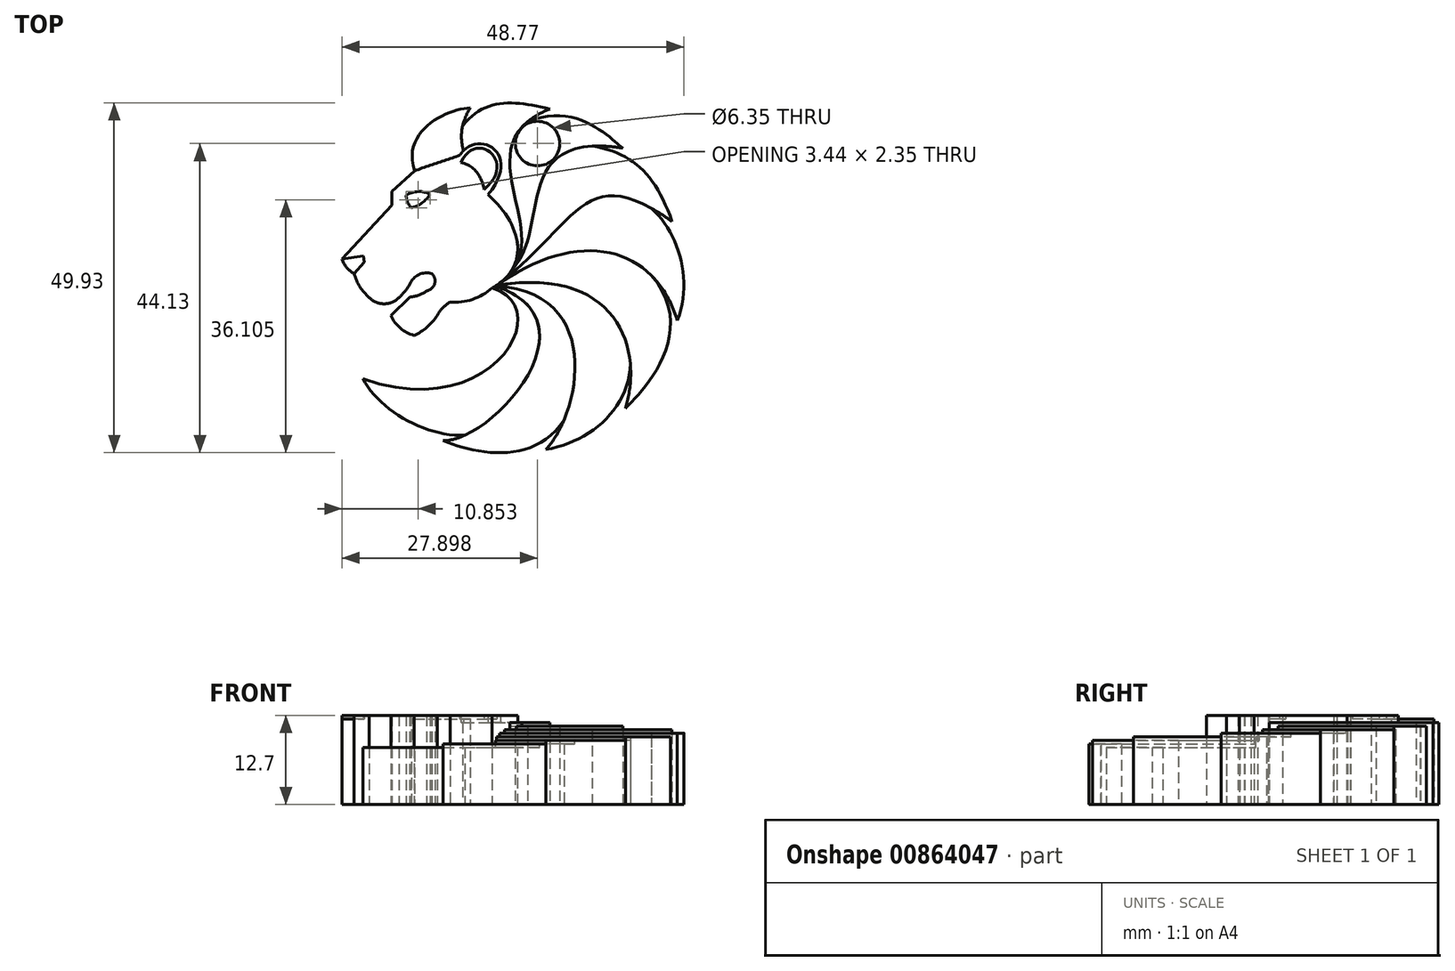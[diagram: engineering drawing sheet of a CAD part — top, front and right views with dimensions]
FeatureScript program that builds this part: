
annotation { "Feature Type Name" : "Feature", "Feature Type Description" : "" }
export const myFeature = defineFeature(function(context is Context, id is Id, definition is map)
    precondition{}
    {
        {
            var Q0;
            Q0=qCreatedBy(makeId("Top.planeOp"),FACE);
            var sketch = newSketch(context, id + "F0", { "sketchPlane" : qUnion([Q0])});
            skFitSpline(sketch, "E0", {"points": [v(-11.17, 15.49) * mm, v(-3.2, 24.48) * mm], "startDerivative": vector(-5.74, 17.74) * mm, "endDerivative": vector(9.44, 0.42) * mm});
            skFitSpline(sketch, "E1", {"points": [v(-3.2, 24.48) * mm, v(-4.16, 18.37) * mm], "startDerivative": vector(-4.63, -7.44) * mm, "endDerivative": vector(1.4, -4.65) * mm});
            skFitSpline(sketch, "E2", {"points": [v(-4.3, 21.92) * mm, v(8.12, 24.3) * mm], "startDerivative": vector(9.68, 12.41) * mm, "endDerivative": vector(14.74, -3.6) * mm});
            skFitSpline(sketch, "E3", {"points": [v(8.12, 24.3) * mm, v(2.46, 0.93) * mm], "startDerivative": vector(-37.26, -15.04) * mm, "endDerivative": vector(-17.73, -19.22) * mm});
            skFitSpline(sketch, "E4", {"points": [v(4.97, 22.5) * mm, v(18.56, 18.74) * mm], "startDerivative": vector(22.85, 9.47) * mm, "endDerivative": vector(2.68, -1.02) * mm});
            skFitSpline(sketch, "E5", {"points": [v(18.56, 18.74) * mm, v(3.37, 2.21) * mm], "startDerivative": vector(-47.21, 7.34) * mm, "endDerivative": vector(-13.68, -17.2) * mm});
            skFitSpline(sketch, "E6", {"points": [v(14.17, 19) * mm, v(25.57, 8.25) * mm], "startDerivative": vector(17.93, -2.85) * mm, "endDerivative": vector(7.02, -19.74) * mm});
            skFitSpline(sketch, "E7", {"points": [v(25.57, 8.25) * mm, v(1.63, 0) * mm], "startDerivative": vector(-37.02, 26.3) * mm, "endDerivative": vector(-32, -25.23) * mm});
            skFitSpline(sketch, "E8", {"points": [v(22.65, 10.13) * mm, v(26.33, -5.88) * mm], "startDerivative": vector(11.59, -10.64) * mm, "endDerivative": vector(-6.75, -17.65) * mm});
            skFitSpline(sketch, "E9", {"points": [v(26.33, -5.88) * mm, v(0.53, -0.85) * mm], "startDerivative": vector(-9.04, 30.15) * mm, "endDerivative": vector(-37.82, -26.43) * mm});
            skFitSpline(sketch, "E10", {"points": [v(22.63, 0.55) * mm, v(18.92, -18.4) * mm], "startDerivative": vector(21.92, -25.56) * mm, "endDerivative": vector(-4.38, -4.47) * mm});
            skFitSpline(sketch, "E11", {"points": [v(18.92, -18.4) * mm, v(0.51, -0.86) * mm], "startDerivative": vector(7.83, 25) * mm, "endDerivative": vector(-52.23, -8.41) * mm});
            skFitSpline(sketch, "E12", {"points": [v(19.61, -12) * mm, v(7.6, -24.27) * mm], "startDerivative": vector(-0.32, -19.2) * mm, "endDerivative": vector(-18.73, -3.03) * mm});
            skFitSpline(sketch, "E13", {"points": [v(7.6, -24.27) * mm, v(0.41, -0.93) * mm], "startDerivative": vector(14.87, 16.04) * mm, "endDerivative": vector(-46.34, 2.64) * mm});
            skFitSpline(sketch, "E14", {"points": [v(10.15, -20.1) * mm, v(-7.07, -23.03) * mm], "startDerivative": vector(-12.89, -19.52) * mm, "endDerivative": vector(-14.06, 5.82) * mm});
            skFitSpline(sketch, "E15", {"points": [v(-7.07, -23.03) * mm, v(0.38, -0.96) * mm], "startDerivative": vector(21.2, -0.2) * mm, "endDerivative": vector(-44.64, 14.98) * mm});
            skFitSpline(sketch, "E16", {"points": [v(-18.51, -14.19) * mm, v(-4, -22.26) * mm], "startDerivative": vector(6.81, -13.35) * mm, "endDerivative": vector(16.4, 0.89) * mm});
            skFitSpline(sketch, "E17", {"points": [v(-18.51, -14.19) * mm, v(-0.1, -1.23) * mm], "startDerivative": vector(55.54, -19.7) * mm, "endDerivative": vector(-28.08, 7.97) * mm});
            skLineSegment(sketch, "E18", {"start": v(-14.38, 10.58) * mm, "end": v(-21.51, 2.89) * mm});
            skLineSegment(sketch, "E19", {"start": v(-14.38, 10.58) * mm, "end": v(-14.38, 12.56) * mm});
            skLineSegment(sketch, "E20", {"start": v(-14.38, 12.56) * mm, "end": v(-11.17, 15.49) * mm});
            skLineSegment(sketch, "E21", {"start": v(-14.52, -5.17) * mm, "end": v(-11.79, -2.52) * mm});
            skArc(sketch, "E22", {"start": v(-12.38, 12) * mm, "mid": v(-12.16, 11.04) * mm, "end": v(-11.67, 10.18) * mm});
            skArc(sketch, "E23", {"start": v(-11.67, 10.18) * mm, "mid": v(-10.11, 10.9) * mm, "end": v(-8.94, 12.15) * mm});
            skArc(sketch, "E24", {"start": v(-8.94, 12.15) * mm, "mid": v(-10.68, 12.53) * mm, "end": v(-12.38, 12) * mm});
            skArc(sketch, "E25", {"start": v(-21.51, 2.89) * mm, "mid": v(-20.84, 1.7) * mm, "end": v(-19.78, 0.83) * mm});
            skArc(sketch, "E26", {"start": v(-19.78, 0.83) * mm, "mid": v(-18.95, -1.05) * mm, "end": v(-17.61, -2.61) * mm});
            skArc(sketch, "E27", {"start": v(-17.61, -2.61) * mm, "mid": v(-15.5, -3.5) * mm, "end": v(-13.39, -2.61) * mm});
            skArc(sketch, "E28", {"start": v(-14.52, -5.17) * mm, "mid": v(-13.2, -6.97) * mm, "end": v(-11.22, -8) * mm});
            skArc(sketch, "E29", {"start": v(-11.22, -8) * mm, "mid": v(-9.37, -6.83) * mm, "end": v(-7.94, -5.17) * mm});
            skArc(sketch, "E30", {"start": v(-6.1, -3.27) * mm, "mid": v(-7.15, -4.1) * mm, "end": v(-7.94, -5.17) * mm});
            skArc(sketch, "E31", {"start": v(-6.1, -3.27) * mm, "mid": v(-2.89, -2.86) * mm, "end": v(-0.1, -1.23) * mm});
            skArc(sketch, "E32", {"start": v(-13.39, -2.61) * mm, "mid": v(-12.54, -1.7) * mm, "end": v(-11.84, -0.7) * mm});
            skArc(sketch, "E33", {"start": v(-8.67, 0.8) * mm, "mid": v(-10.54, 0.68) * mm, "end": v(-11.84, -0.7) * mm});
            skArc(sketch, "E34", {"start": v(-9.44, -1.65) * mm, "mid": v(-8.3, -0.66) * mm, "end": v(-8.67, 0.8) * mm});
            skArc(sketch, "E35", {"start": v(-11.79, -2.52) * mm, "mid": v(-10.55, -2.26) * mm, "end": v(-9.44, -1.65) * mm});
            skFitSpline(sketch, "E36", {"points": [v(-0.1, -1.23) * mm, v(-0.7, 12.08) * mm], "startDerivative": vector(17.47, 9.64) * mm, "endDerivative": vector(-13.78, 11.7) * mm});
            skFitSpline(sketch, "E37", {"points": [v(-11.17, 15.49) * mm, v(-4.66, 17.73) * mm], "startDerivative": vector(6.4, 2.3) * mm, "endDerivative": vector(6.4, 2.3) * mm});
            skLineSegment(sketch, "E38", {"start": v(-21.51, 2.89) * mm, "end": v(-18.44, 3.32) * mm});
            skLineSegment(sketch, "E39", {"start": v(-18.44, 3.32) * mm, "end": v(-18.32, 2.44) * mm});
            skLineSegment(sketch, "E40", {"start": v(-18.32, 2.44) * mm, "end": v(-19.78, 0.83) * mm});
            skLineSegment(sketch, "E41", {"start": v(-18.44, 3.32) * mm, "end": v(-11.67, 10.18) * mm});
            skFitSpline(sketch, "E42", {"points": [v(-5.1, 16.82) * mm, v(-0.7, 12.08) * mm], "startDerivative": vector(5.58, 15.8) * mm, "endDerivative": vector(-16.44, -19.38) * mm});
            skFitSpline(sketch, "E43", {"points": [v(-4.56, 16.67) * mm, v(-1.23, 12.83) * mm], "startDerivative": vector(6.77, 14.53) * mm, "endDerivative": vector(-14.42, -11.84) * mm});
            skFitSpline(sketch, "E44", {"points": [v(-4.56, 16.67) * mm, v(-1.23, 12.83) * mm], "startDerivative": vector(6.2, -1.24) * mm, "endDerivative": vector(0.83, -4.86) * mm});
            skPoint(sketch, "E45", {"position": v(6.39, 19.38) * mm});
            skSolve(sketch);
        }
        {
            var Q0;
            Q0=makeQuery(id+"F0.imprint","IMPRINT",FACE,{"disambiguationData":[TD([[makeQuery(id+"F0.imprint","IMPRINT",EDGE,{"derivedFrom":sQuery(id+"F0.wireOp",EDGE,"E18")}),1.0]])]});
            extrude(context, id + "F1", {"entities" : qUnion([Q0]), "depth" : 12.7 * mm, "offsetDistance" : 25.4 * mm});
        }
        {
            var Q0;
            {var subQ4=sQuery(id+"F0.wireOp",EDGE,"E0");Q0=makeQuery(id+"F0.imprint","IMPRINT",FACE,{"disambiguationData":[TD([[makeQuery(id+"F0.imprint","IMPRINT",EDGE,{"derivedFrom":subQ4}),-1.0]])]});}
            var Q1;
            Q1=makeQuery(id+"F0.imprint","IMPRINT",FACE,{"disambiguationData":[TD([[makeQuery(id+"F0.imprint","IMPRINT",EDGE,{"derivedFrom":sQuery(id+"F0.wireOp",EDGE,"E43")}),-1.0]])]});
            var Q2;
            Q2=makeQuery(id+"F0.imprint","IMPRINT",FACE,{"disambiguationData":[TD([[makeQuery(id+"F0.imprint","IMPRINT",EDGE,{"derivedFrom":sQuery(id+"F0.wireOp",EDGE,"E25")}),1.0]])]});
            extrude(context, id + "F2", {"entities" : qUnion([Q0, Q1, Q2]), "operationType" : NewBodyOperationType.ADD, "depth" : 12.2 * mm, "offsetDistance" : 25.4 * mm});
        }
        {
            var Q0;
            {var subQ3=sQuery(id+"F0.wireOp",EDGE,"E2");Q0=makeQuery(id+"F0.imprint","IMPRINT",FACE,{"disambiguationData":[TD([[makeQuery(id+"F0.imprint","IMPRINT",EDGE,{"derivedFrom":subQ3}),-1.0]])]});}
            extrude(context, id + "F3", {"entities" : qUnion([Q0]), "operationType" : NewBodyOperationType.ADD, "depth" : 11.68 * mm, "offsetDistance" : 25.4 * mm});
        }
        {
            var Q0;
            {var subQ0=sQuery(id+"F0.wireOp",EDGE,"E4");Q0=makeQuery(id+"F0.imprint","IMPRINT",FACE,{"disambiguationData":[TD([[makeQuery(id+"F0.imprint","IMPRINT",EDGE,{"derivedFrom":subQ0}),-1.0]])]});}
            extrude(context, id + "F4", {"entities" : qUnion([Q0]), "operationType" : NewBodyOperationType.ADD, "depth" : 11.18 * mm, "offsetDistance" : 25.4 * mm});
        }
        {
            var Q0;
            {var subQ0=sQuery(id+"F0.wireOp",EDGE,"E6");Q0=makeQuery(id+"F0.imprint","IMPRINT",FACE,{"disambiguationData":[TD([[makeQuery(id+"F0.imprint","IMPRINT",EDGE,{"derivedFrom":subQ0}),-1.0]])]});}
            extrude(context, id + "F5", {"entities" : qUnion([Q0]), "operationType" : NewBodyOperationType.ADD, "depth" : 10.67 * mm, "offsetDistance" : 25.4 * mm});
        }
        {
            var Q0;
            {var subQ4=sQuery(id+"F0.wireOp",EDGE,"E8");Q0=makeQuery(id+"F0.imprint","IMPRINT",FACE,{"disambiguationData":[TD([[makeQuery(id+"F0.imprint","IMPRINT",EDGE,{"derivedFrom":subQ4}),-1.0]])]});}
            extrude(context, id + "F6", {"entities" : qUnion([Q0]), "operationType" : NewBodyOperationType.ADD, "depth" : 10.16 * mm, "offsetDistance" : 25.4 * mm});
        }
        {
            var Q0;
            {var subQ4=sQuery(id+"F0.wireOp",EDGE,"E10");Q0=makeQuery(id+"F0.imprint","IMPRINT",FACE,{"disambiguationData":[TD([[makeQuery(id+"F0.imprint","IMPRINT",EDGE,{"derivedFrom":subQ4}),-1.0]])]});}
            extrude(context, id + "F7", {"entities" : qUnion([Q0]), "operationType" : NewBodyOperationType.ADD, "depth" : 9.65 * mm, "offsetDistance" : 25.4 * mm});
        }
        {
            var Q0;
            {var subQ4=sQuery(id+"F0.wireOp",EDGE,"E12");Q0=makeQuery(id+"F0.imprint","IMPRINT",FACE,{"disambiguationData":[TD([[makeQuery(id+"F0.imprint","IMPRINT",EDGE,{"derivedFrom":subQ4}),-1.0]])]});}
            extrude(context, id + "F8", {"entities" : qUnion([Q0]), "operationType" : NewBodyOperationType.ADD, "depth" : 9.14 * mm, "offsetDistance" : 25.4 * mm});
        }
        {
            var Q0;
            {var subQ6=sQuery(id+"F0.wireOp",EDGE,"E14");Q0=makeQuery(id+"F0.imprint","IMPRINT",FACE,{"disambiguationData":[TD([[makeQuery(id+"F0.imprint","IMPRINT",EDGE,{"derivedFrom":subQ6}),-1.0]])]});}
            extrude(context, id + "F9", {"entities" : qUnion([Q0]), "operationType" : NewBodyOperationType.ADD, "depth" : 8.64 * mm, "offsetDistance" : 25.4 * mm});
        }
        {
            var Q0;
            {var subQ3=sQuery(id+"F0.wireOp",EDGE,"E16");Q0=makeQuery(id+"F0.imprint","IMPRINT",FACE,{"disambiguationData":[TD([[makeQuery(id+"F0.imprint","IMPRINT",EDGE,{"derivedFrom":subQ3}),1.0]])]});}
            extrude(context, id + "F10", {"entities" : qUnion([Q0]), "operationType" : NewBodyOperationType.ADD, "depth" : 8.13 * mm, "offsetDistance" : 25.4 * mm});
        }
        {
            var Q0;
            Q0=sQuery(id+"F0.wireOp",VERTEX,"E45");
            var Q1;
            Q1=makeQuery(id+"F1.opExtrude","SWEPT_BODY",BODY,{"disambiguationData":[OSD([sQuery(id+"F0.wireOp",EDGE,"E18"),sQuery(id+"F0.wireOp",EDGE,"E19"),sQuery(id+"F0.wireOp",EDGE,"E20"),sQuery(id+"F0.wireOp",EDGE,"E21"),sQuery(id+"F0.wireOp",EDGE,"E22"),sQuery(id+"F0.wireOp",EDGE,"E23"),sQuery(id+"F0.wireOp",EDGE,"E24"),sQuery(id+"F0.wireOp",EDGE,"E26"),sQuery(id+"F0.wireOp",EDGE,"E27"),sQuery(id+"F0.wireOp",EDGE,"E28"),sQuery(id+"F0.wireOp",EDGE,"E29"),sQuery(id+"F0.wireOp",EDGE,"E30"),sQuery(id+"F0.wireOp",EDGE,"E31"),sQuery(id+"F0.wireOp",EDGE,"E32"),sQuery(id+"F0.wireOp",EDGE,"E33"),sQuery(id+"F0.wireOp",EDGE,"E34"),sQuery(id+"F0.wireOp",EDGE,"E35"),sQuery(id+"F0.wireOp",EDGE,"E36"),sQuery(id+"F0.wireOp",EDGE,"E37"),sQuery(id+"F0.wireOp",EDGE,"E38"),sQuery(id+"F0.wireOp",EDGE,"E39"),sQuery(id+"F0.wireOp",EDGE,"E40"),sQuery(id+"F0.wireOp",EDGE,"E42"),sQuery(id+"F0.wireOp",EDGE,"E43"),sQuery(id+"F0.wireOp",EDGE,"E44")])]});
            hole(context, id + "F11", {"style" : HoleStyle.SIMPLE, "endStyle" : HoleEndStyle.THROUGH, "oppositeDirection" : true, "holeDiameter" : 6.35 * mm, "majorDiameter" : 6.35 * mm, "isTappedThrough" : true, "tappedDepth" : 12.7 * mm, "tapClearance" : 3, "locations" : qUnion([Q0]), "scope" : qUnion([Q1])});
        }
    });
